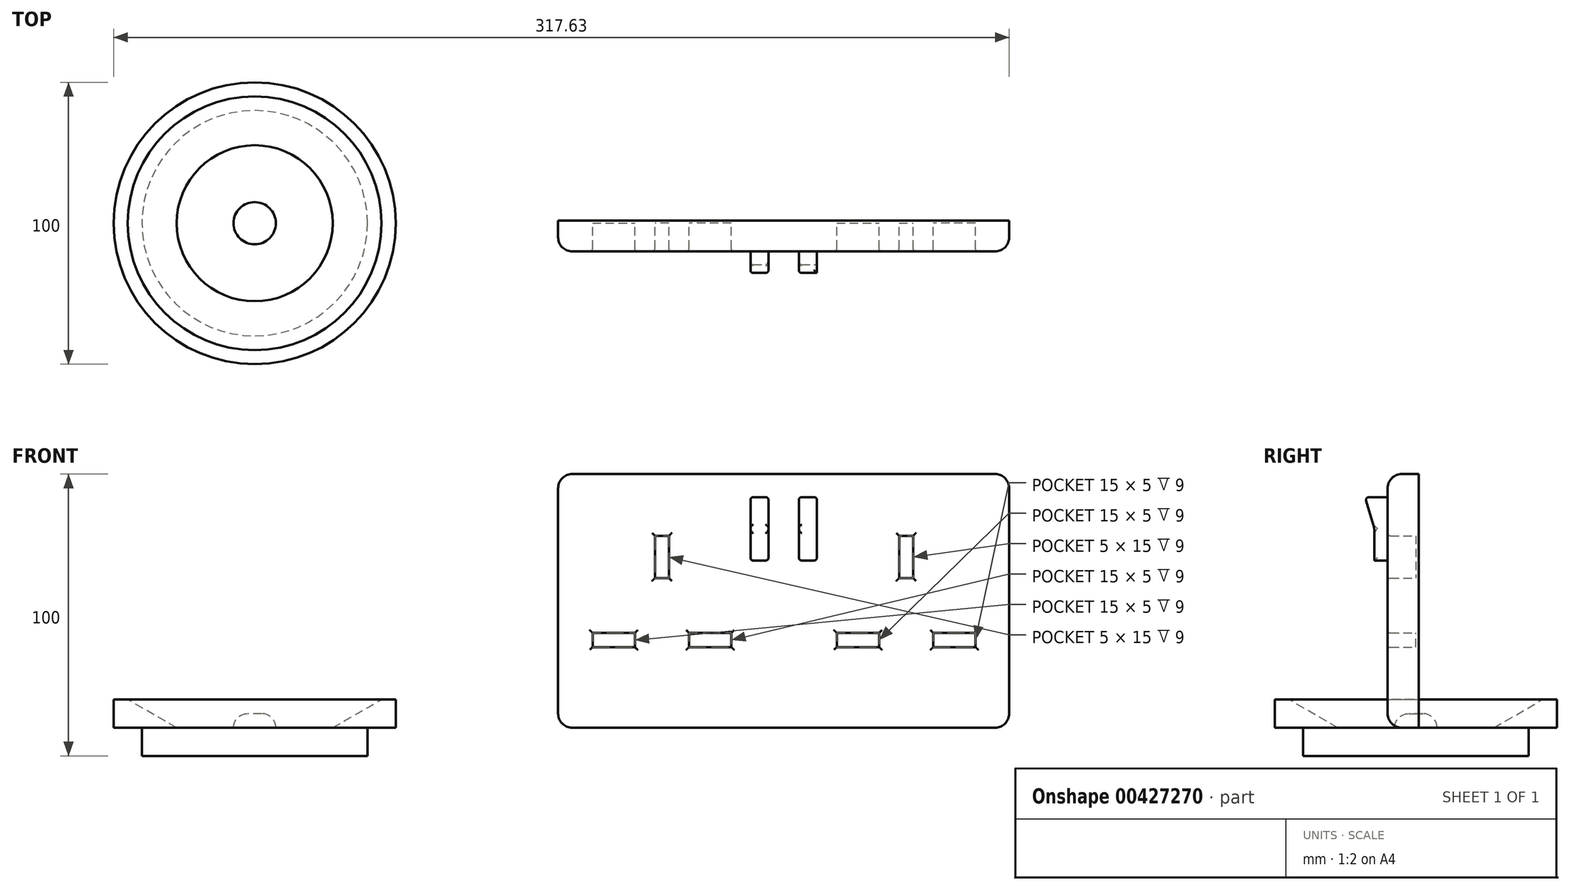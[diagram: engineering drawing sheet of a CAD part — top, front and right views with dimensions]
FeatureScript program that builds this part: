
annotation { "Feature Type Name" : "Feature", "Feature Type Description" : "" }
export const myFeature = defineFeature(function(context is Context, id is Id, definition is map)
    precondition{}
    {
        {
            var Q0;
            Q0=qCreatedBy(makeId("Top.planeOp"),FACE);
            var sketch = newSketch(context, id + "F0", { "sketchPlane" : qUnion([Q0])});
            skCircle(sketch, "E0", {"center": v(0, 0) * mm, "radius": 50 * mm});
            skSolve(sketch);
        }
        {
            var Q0;
            Q0 = qSketchRegion(id + "F0", true);
            extrude(context, id + "F1", {"entities" : qUnion([Q0]), "depth" : 10 * mm, "offsetDistance" : 25 * mm});
        }
        {
            var Q0;
            Q0=makeQuery(id+"F1.opExtrude","CAP_FACE",FACE,{"disambiguationData":[OSD([sQuery(id+"F0.wireOp",EDGE,"E0")])],"isStart":true});
            var sketch = newSketch(context, id + "F2", { "sketchPlane" : qUnion([Q0])});
            skCircle(sketch, "E1", {"center": v(0, 0) * mm, "radius": 40 * mm});
            skSolve(sketch);
        }
        {
            var Q0;
            Q0 = qSketchRegion(id + "F2", true);
            extrude(context, id + "F3", {"entities" : qUnion([Q0]), "operationType" : NewBodyOperationType.ADD, "depth" : 10 * mm, "offsetDistance" : 25 * mm});
        }
        {
            var Q0;
            Q0=makeQuery(id+"F1.opExtrude","CAP_FACE",FACE,{"disambiguationData":[OSD([sQuery(id+"F0.wireOp",EDGE,"E0")])],"isStart":false});
            var sketch = newSketch(context, id + "F4", { "sketchPlane" : qUnion([Q0])});
            skCircle(sketch, "E2", {"center": v(0, 0) * mm, "radius": 45 * mm});
            skSolve(sketch);
        }
        {
            var Q0;
            Q0 = qSketchRegion(id + "F4", true);
            extrude(context, id + "F5", {"entities" : qUnion([Q0]), "operationType" : NewBodyOperationType.REMOVE, "oppositeDirection" : true, "depth" : 10 * mm, "offsetDistance" : 25 * mm, "hasDraft" : true, "draftAngle" : 60 * degree, "draftPullDirection" : true});
        }
        {
            var Q0;
            Q0=makeQuery(id+"F5.boolean.opBoolean","COPY",FACE,{"derivedFrom":makeQuery(id+"F5.opExtrude","CAP_FACE",FACE,{"disambiguationData":[OSD([sQuery(id+"F4.wireOp",EDGE,"E2")])],"isStart":false})});
            var sketch = newSketch(context, id + "F6", { "sketchPlane" : qUnion([Q0])});
            skCircle(sketch, "E3", {"center": v(0, 0) * mm, "radius": 7.5 * mm});
            skSolve(sketch);
        }
        {
            var Q0;
            Q0 = qSketchRegion(id + "F6", true);
            extrude(context, id + "F7", {"entities" : qUnion([Q0]), "operationType" : NewBodyOperationType.ADD, "depth" : 5 * mm, "offsetDistance" : 25 * mm});
        }
        {
            var Q0;
            Q0=makeQuery(id+"F7.opExtrude","CAP_EDGE",EDGE,{"disambiguationData":[OSD([sQuery(id+"F6.wireOp",EDGE,"E3")])],"isStart":false});
            fillet(context, id + "F8", {"entities" : qUnion([Q0]), "radius" : 5 * mm, "tangentPropagation" : true, "allowEdgeOverflow" : false});
        }
        {
            var Q0;
            Q0=qCreatedBy(makeId("Front.planeOp"),FACE);
            var sketch = newSketch(context, id + "F9", { "sketchPlane" : qUnion([Q0])});
            skLineSegment(sketch, "E4.bottom", {"start": v(107.63, 0) * mm, "end": v(267.63, 0) * mm});
            skLineSegment(sketch, "E4.top", {"start": v(107.63, 90) * mm, "end": v(267.63, 90) * mm});
            skLineSegment(sketch, "E4.left", {"start": v(107.63, 0) * mm, "end": v(107.63, 90) * mm});
            skLineSegment(sketch, "E4.right", {"start": v(267.63, 0) * mm, "end": v(267.63, 90) * mm});
            skSolve(sketch);
        }
        {
            var Q0;
            Q0 = qSketchRegion(id + "F9", true);
            extrude(context, id + "F10", {"entities" : qUnion([Q0]), "depth" : 10 * mm, "offsetDistance" : 25 * mm});
        }
        {
            var Q0;
            Q0=qCreatedBy(makeId("Front.planeOp"),FACE);
            var sketch = newSketch(context, id + "F11", { "sketchPlane" : qUnion([Q0])});
            skLineSegment(sketch, "E5.bottom", {"start": v(146.96, 68.1) * mm, "end": v(141.96, 68.1) * mm});
            skLineSegment(sketch, "E5.top", {"start": v(146.96, 53.1) * mm, "end": v(141.96, 53.1) * mm});
            skLineSegment(sketch, "E5.left", {"start": v(146.96, 68.1) * mm, "end": v(146.96, 53.1) * mm});
            skLineSegment(sketch, "E5.right", {"start": v(141.96, 68.1) * mm, "end": v(141.96, 53.1) * mm});
            skPoint(sketch, "E5.middle", {"position": v(144.46, 60.6) * mm});
            skLineSegment(sketch, "E6.bottom", {"start": v(119.85, 28.62) * mm, "end": v(134.85, 28.62) * mm});
            skLineSegment(sketch, "E6.top", {"start": v(119.85, 33.62) * mm, "end": v(134.85, 33.62) * mm});
            skLineSegment(sketch, "E6.left", {"start": v(119.85, 28.62) * mm, "end": v(119.85, 33.62) * mm});
            skLineSegment(sketch, "E6.right", {"start": v(134.85, 28.62) * mm, "end": v(134.85, 33.62) * mm});
            skPoint(sketch, "E6.middle", {"position": v(127.35, 31.12) * mm});
            skLineSegment(sketch, "E7.bottom", {"start": v(169.06, 28.62) * mm, "end": v(154.06, 28.62) * mm});
            skLineSegment(sketch, "E7.top", {"start": v(169.06, 33.62) * mm, "end": v(154.06, 33.62) * mm});
            skLineSegment(sketch, "E7.left", {"start": v(169.06, 28.62) * mm, "end": v(169.06, 33.62) * mm});
            skLineSegment(sketch, "E7.right", {"start": v(154.06, 28.62) * mm, "end": v(154.06, 33.62) * mm});
            skPoint(sketch, "E7.middle", {"position": v(161.56, 31.12) * mm});
            skPoint(sketch, "E8", {"position": v(134.85, 31.12) * mm});
            skLineSegment(sketch, "E9.MirrorCS", {"start": v(228.58, 68.1) * mm, "end": v(228.58, 53.1) * mm});
            skLineSegment(sketch, "E10.MirrorCS", {"start": v(228.58, 68.1) * mm, "end": v(233.58, 68.1) * mm});
            skLineSegment(sketch, "E11.MirrorCS", {"start": v(233.58, 68.1) * mm, "end": v(233.58, 53.1) * mm});
            skLineSegment(sketch, "E12.MirrorCS", {"start": v(228.58, 53.1) * mm, "end": v(233.58, 53.1) * mm});
            skLineSegment(sketch, "E13.MirrorCS", {"start": v(206.47, 28.62) * mm, "end": v(221.47, 28.62) * mm});
            skLineSegment(sketch, "E14.MirrorCS", {"start": v(206.47, 33.62) * mm, "end": v(221.47, 33.62) * mm});
            skLineSegment(sketch, "E15.MirrorCS", {"start": v(221.47, 28.62) * mm, "end": v(221.47, 33.62) * mm});
            skLineSegment(sketch, "E16.MirrorCS", {"start": v(206.47, 28.62) * mm, "end": v(206.47, 33.62) * mm});
            skPoint(sketch, "E17.MirrorP", {"position": v(213.97, 31.12) * mm});
            skLineSegment(sketch, "E18.MirrorCS", {"start": v(240.68, 28.62) * mm, "end": v(240.68, 33.62) * mm});
            skLineSegment(sketch, "E19.MirrorCS", {"start": v(255.68, 28.62) * mm, "end": v(255.68, 33.62) * mm});
            skLineSegment(sketch, "E20.MirrorCS", {"start": v(255.68, 28.62) * mm, "end": v(240.68, 28.62) * mm});
            skLineSegment(sketch, "E21.MirrorCS", {"start": v(255.68, 33.62) * mm, "end": v(240.68, 33.62) * mm});
            skPoint(sketch, "E22.MirrorP", {"position": v(248.18, 31.12) * mm});
            skPoint(sketch, "E23.MirrorP", {"position": v(240.68, 31.12) * mm});
            skSolve(sketch);
        }
        {
            var Q0;
            Q0 = qSketchRegion(id + "F11", true);
            extrude(context, id + "F12", {"entities" : qUnion([Q0]), "operationType" : NewBodyOperationType.REMOVE, "depth" : 15 * mm, "offsetDistance" : 25 * mm});
        }
        {
            var Q0;
            Q0=makeQuery(id+"F10.opExtrude","CAP_FACE",FACE,{"disambiguationData":[OSD([sQuery(id+"F9.wireOp",EDGE,"E4.bottom"),sQuery(id+"F9.wireOp",EDGE,"E4.top"),sQuery(id+"F9.wireOp",EDGE,"E4.left"),sQuery(id+"F9.wireOp",EDGE,"E4.right")])],"isStart":false});
            var sketch = newSketch(context, id + "F13", { "sketchPlane" : qUnion([Q0])});
            skLineSegment(sketch, "E24.bottom", {"start": v(193.04, 81.81) * mm, "end": v(199.4, 81.81) * mm});
            skLineSegment(sketch, "E24.top", {"start": v(193.04, 59.31) * mm, "end": v(199.4, 59.31) * mm});
            skLineSegment(sketch, "E24.left", {"start": v(193.04, 81.81) * mm, "end": v(193.04, 59.31) * mm});
            skLineSegment(sketch, "E24.right", {"start": v(199.4, 81.81) * mm, "end": v(199.4, 59.31) * mm});
            skLineSegment(sketch, "E25.MirrorCS", {"start": v(182.22, 81.81) * mm, "end": v(175.86, 81.81) * mm});
            skLineSegment(sketch, "E26.MirrorCS", {"start": v(182.22, 81.81) * mm, "end": v(182.22, 59.31) * mm});
            skLineSegment(sketch, "E27.MirrorCS", {"start": v(175.86, 81.81) * mm, "end": v(175.86, 59.31) * mm});
            skLineSegment(sketch, "E28.MirrorCS", {"start": v(182.22, 59.31) * mm, "end": v(175.86, 59.31) * mm});
            skSolve(sketch);
        }
        {
            var Q0;
            Q0 = qSketchRegion(id + "F13", true);
            extrude(context, id + "F14", {"entities" : qUnion([Q0]), "operationType" : NewBodyOperationType.ADD, "depth" : 8 * mm, "offsetDistance" : 25 * mm});
        }
        {
            var Q0;
            Q0=makeQuery(id+"F14.opExtrude","SWEPT_FACE",FACE,{"disambiguationData":[OSD([sQuery(id+"F13.wireOp",EDGE,"E24.right")])]});
            var sketch = newSketch(context, id + "F15", { "sketchPlane" : qUnion([Q0])});
            skLineSegment(sketch, "E29", {"start": v(-14.66, 70.56) * mm, "end": v(-18, 81.81) * mm});
            skLineSegment(sketch, "E30", {"start": v(-14.66, 70.56) * mm, "end": v(-14.66, 59.31) * mm});
            skPoint(sketch, "E30.endSnap0", {"position": v(-14, 59.31) * mm});
            skLineSegment(sketch, "E31", {"start": v(-14.66, 59.31) * mm, "end": v(-18, 59.31) * mm});
            skLineSegment(sketch, "E32", {"start": v(-18, 59.31) * mm, "end": v(-18, 81.81) * mm});
            skSolve(sketch);
        }
        {
            var Q0;
            Q0 = qSketchRegion(id + "F15", true);
            extrude(context, id + "F16", {"entities" : qUnion([Q0]), "operationType" : NewBodyOperationType.REMOVE, "oppositeDirection" : true, "depth" : 25 * mm, "offsetDistance" : 25 * mm});
        }
        {
            var Q0;
            Q0=makeQuery(id+"F16.boolean.opBoolean","COPY",EDGE,{"derivedFrom":makeQuery(id+"F16.opExtrude","CAP_EDGE",EDGE,{"disambiguationData":[OSD([sQuery(id+"F15.wireOp",EDGE,"E30")])],"isStart":true})});
            var Q1;
            Q1=makeQuery(id+"F16.boolean.opBoolean","COPY",EDGE,{"derivedFrom":makeQuery(id+"F16.opExtrude","CAP_EDGE",EDGE,{"disambiguationData":[OSD([sQuery(id+"F15.wireOp",EDGE,"E29")])],"isStart":true})});
            var Q2;
            {var subQ0=sQuery(id+"F13.wireOp",EDGE,"E24.bottom");Q2=makeQuery(id+"F16.boolean.opBoolean","MERGE",EDGE,{"derivedFrom":[makeQuery(id+"F14.opExtrude","CAP_EDGE",EDGE,{"disambiguationData":[OSD([subQ0])],"isStart":false}),makeQuery(id+"F16.opExtrude","SWEPT_EDGE",EDGE,{"disambiguationData":[OSD([subQ0,sQuery(id+"F13.wireOp",EDGE,"E24.right"),sQuery(id+"F15.wireOp",EDGE,"E29"),sQuery(id+"F15.wireOp",EDGE,"E32")])]})]});}
            var Q3;
            Q3=makeQuery(id+"F16.boolean.opBoolean","INTERSECT",EDGE,{"derivedFrom":[makeQuery(id+"F14.opExtrude","SWEPT_FACE",FACE,{"disambiguationData":[OSD([sQuery(id+"F13.wireOp",EDGE,"E24.left")])]}),makeQuery(id+"F16.opExtrude","SWEPT_FACE",FACE,{"disambiguationData":[OSD([sQuery(id+"F15.wireOp",EDGE,"E29")])]})]});
            var Q4;
            Q4=makeQuery(id+"F16.boolean.opBoolean","INTERSECT",EDGE,{"derivedFrom":[makeQuery(id+"F14.opExtrude","SWEPT_FACE",FACE,{"disambiguationData":[OSD([sQuery(id+"F13.wireOp",EDGE,"E24.left")])]}),makeQuery(id+"F16.opExtrude","SWEPT_FACE",FACE,{"disambiguationData":[OSD([sQuery(id+"F15.wireOp",EDGE,"E30")])]})]});
            var Q5;
            {var subQ0=sQuery(id+"F13.wireOp",EDGE,"E24.top");var subQ1=sQuery(id+"F15.wireOp",EDGE,"E30");Q5=makeQuery(id+"F16.boolean.opBoolean","COPY",EDGE,{"disambiguationData":[topologyDisambiguationEdgeConnected([makeQuery(id+"F14.opExtrude","SWEPT_FACE",FACE,{"disambiguationData":[OSD([subQ0])]})])],"derivedFrom":makeQuery(id+"F16.opExtrude","SWEPT_EDGE",EDGE,{"disambiguationData":[OSD([subQ0,sQuery(id+"F13.wireOp",EDGE,"E24.right"),subQ1,sQuery(id+"F15.wireOp",EDGE,"E31")])]})});}
            var Q6;
            Q6=makeQuery(id+"F14.opExtrude","SWEPT_EDGE",EDGE,{"disambiguationData":[OSD([sQuery(id+"F13.wireOp",EDGE,"E24.bottom"),sQuery(id+"F13.wireOp",EDGE,"E24.right")])]});
            var Q7;
            Q7=makeQuery(id+"F14.opExtrude","SWEPT_EDGE",EDGE,{"disambiguationData":[OSD([sQuery(id+"F13.wireOp",EDGE,"E24.top"),sQuery(id+"F13.wireOp",EDGE,"E24.right")])]});
            var Q8;
            Q8=makeQuery(id+"F14.opExtrude","SWEPT_EDGE",EDGE,{"disambiguationData":[OSD([sQuery(id+"F13.wireOp",EDGE,"E24.top"),sQuery(id+"F13.wireOp",EDGE,"E24.left")])]});
            var Q9;
            Q9=makeQuery(id+"F14.opExtrude","SWEPT_EDGE",EDGE,{"disambiguationData":[OSD([sQuery(id+"F13.wireOp",EDGE,"E24.bottom"),sQuery(id+"F13.wireOp",EDGE,"E24.left")])]});
            var Q10;
            Q10=makeQuery(id+"F16.boolean.opBoolean","INTERSECT",EDGE,{"derivedFrom":[makeQuery(id+"F14.opExtrude","SWEPT_FACE",FACE,{"disambiguationData":[OSD([sQuery(id+"F13.wireOp",EDGE,"E26.MirrorCS")])]}),makeQuery(id+"F16.opExtrude","SWEPT_FACE",FACE,{"disambiguationData":[OSD([sQuery(id+"F15.wireOp",EDGE,"E30")])]})]});
            var Q11;
            Q11=makeQuery(id+"F16.boolean.opBoolean","INTERSECT",EDGE,{"derivedFrom":[makeQuery(id+"F14.opExtrude","SWEPT_FACE",FACE,{"disambiguationData":[OSD([sQuery(id+"F13.wireOp",EDGE,"E26.MirrorCS")])]}),makeQuery(id+"F16.opExtrude","SWEPT_FACE",FACE,{"disambiguationData":[OSD([sQuery(id+"F15.wireOp",EDGE,"E29")])]})]});
            var Q12;
            Q12=makeQuery(id+"F16.boolean.opBoolean","MERGE",EDGE,{"derivedFrom":[makeQuery(id+"F14.opExtrude","CAP_EDGE",EDGE,{"disambiguationData":[OSD([sQuery(id+"F13.wireOp",EDGE,"E25.MirrorCS")])],"isStart":false}),makeQuery(id+"F16.opExtrude","SWEPT_EDGE",EDGE,{"disambiguationData":[OSD([sQuery(id+"F13.wireOp",EDGE,"E24.bottom"),sQuery(id+"F13.wireOp",EDGE,"E24.right"),sQuery(id+"F15.wireOp",EDGE,"E29"),sQuery(id+"F15.wireOp",EDGE,"E32")])]})]});
            var Q13;
            Q13=makeQuery(id+"F16.boolean.opBoolean","INTERSECT",EDGE,{"derivedFrom":[makeQuery(id+"F14.opExtrude","SWEPT_FACE",FACE,{"disambiguationData":[OSD([sQuery(id+"F13.wireOp",EDGE,"E27.MirrorCS")])]}),makeQuery(id+"F16.opExtrude","SWEPT_FACE",FACE,{"disambiguationData":[OSD([sQuery(id+"F15.wireOp",EDGE,"E29")])]})]});
            var Q14;
            Q14=makeQuery(id+"F16.boolean.opBoolean","INTERSECT",EDGE,{"derivedFrom":[makeQuery(id+"F14.opExtrude","SWEPT_FACE",FACE,{"disambiguationData":[OSD([sQuery(id+"F13.wireOp",EDGE,"E27.MirrorCS")])]}),makeQuery(id+"F16.opExtrude","SWEPT_FACE",FACE,{"disambiguationData":[OSD([sQuery(id+"F15.wireOp",EDGE,"E30")])]})]});
            var Q15;
            {var subQ0=sQuery(id+"F15.wireOp",EDGE,"E30");Q15=makeQuery(id+"F16.boolean.opBoolean","COPY",EDGE,{"disambiguationData":[topologyDisambiguationEdgeConnected([makeQuery(id+"F14.opExtrude","SWEPT_FACE",FACE,{"disambiguationData":[OSD([sQuery(id+"F13.wireOp",EDGE,"E28.MirrorCS")])]})])],"derivedFrom":makeQuery(id+"F16.opExtrude","SWEPT_EDGE",EDGE,{"disambiguationData":[OSD([sQuery(id+"F13.wireOp",EDGE,"E24.top"),sQuery(id+"F13.wireOp",EDGE,"E24.right"),subQ0,sQuery(id+"F15.wireOp",EDGE,"E31")])]})});}
            var Q16;
            Q16=makeQuery(id+"F14.opExtrude","SWEPT_EDGE",EDGE,{"disambiguationData":[OSD([sQuery(id+"F13.wireOp",EDGE,"E27.MirrorCS"),sQuery(id+"F13.wireOp",EDGE,"E28.MirrorCS")])]});
            var Q17;
            Q17=makeQuery(id+"F14.opExtrude","SWEPT_EDGE",EDGE,{"disambiguationData":[OSD([sQuery(id+"F13.wireOp",EDGE,"E26.MirrorCS"),sQuery(id+"F13.wireOp",EDGE,"E28.MirrorCS")])]});
            var Q18;
            Q18=makeQuery(id+"F14.opExtrude","SWEPT_EDGE",EDGE,{"disambiguationData":[OSD([sQuery(id+"F13.wireOp",EDGE,"E25.MirrorCS"),sQuery(id+"F13.wireOp",EDGE,"E26.MirrorCS")])]});
            var Q19;
            Q19=makeQuery(id+"F14.opExtrude","SWEPT_EDGE",EDGE,{"disambiguationData":[OSD([sQuery(id+"F13.wireOp",EDGE,"E25.MirrorCS"),sQuery(id+"F13.wireOp",EDGE,"E27.MirrorCS")])]});
            fillet(context, id + "F17", {"entities" : qUnion([Q0, Q1, Q2, Q3, Q4, Q5, Q6, Q7, Q8, Q9, Q10, Q11, Q12, Q13, Q14, Q15, Q16, Q17, Q18, Q19]), "radius" : 1 * mm, "tangentPropagation" : true, "allowEdgeOverflow" : false});
        }
        {
            var Q0;
            {var subQ0=sQuery(id+"F15.wireOp",EDGE,"E29");var subQ1=sQuery(id+"F15.wireOp",EDGE,"E30");Q0=makeQuery(id+"F16.boolean.opBoolean","COPY",EDGE,{"disambiguationData":[TD([makeQuery(id+"F14.opExtrude","SWEPT_FACE",FACE,{"disambiguationData":[OSD([sQuery(id+"F13.wireOp",EDGE,"E26.MirrorCS")])]})])],"derivedFrom":makeQuery(id+"F16.opExtrude","SWEPT_EDGE",EDGE,{"disambiguationData":[OSD([subQ0,subQ1])]})});}
            var Q1;
            {var subQ0=sQuery(id+"F15.wireOp",EDGE,"E29");var subQ1=sQuery(id+"F15.wireOp",EDGE,"E30");Q1=makeQuery(id+"F16.boolean.opBoolean","COPY",EDGE,{"disambiguationData":[TD([makeQuery(id+"F14.opExtrude","SWEPT_FACE",FACE,{"disambiguationData":[OSD([sQuery(id+"F13.wireOp",EDGE,"E24.left")])]})])],"derivedFrom":makeQuery(id+"F16.opExtrude","SWEPT_EDGE",EDGE,{"disambiguationData":[OSD([subQ0,subQ1])]})});}
            fillet(context, id + "F18", {"entities" : qUnion([Q0, Q1]), "radius" : 10 * mm, "tangentPropagation" : true, "allowEdgeOverflow" : false});
        }
        {
            var Q0;
            Q0=makeQuery(id+"F12.boolean.opBoolean","INTERSECT",EDGE,{"derivedFrom":[makeQuery(id+"F10.opExtrude","CAP_FACE",FACE,{"disambiguationData":[OSD([sQuery(id+"F9.wireOp",EDGE,"E4.bottom"),sQuery(id+"F9.wireOp",EDGE,"E4.top"),sQuery(id+"F9.wireOp",EDGE,"E4.left"),sQuery(id+"F9.wireOp",EDGE,"E4.right")])],"isStart":false}),makeQuery(id+"F12.opExtrude","SWEPT_FACE",FACE,{"disambiguationData":[OSD([sQuery(id+"F11.wireOp",EDGE,"E5.right")])]})]});
            var Q1;
            Q1=makeQuery(id+"F12.boolean.opBoolean","INTERSECT",EDGE,{"derivedFrom":[makeQuery(id+"F10.opExtrude","CAP_FACE",FACE,{"disambiguationData":[OSD([sQuery(id+"F9.wireOp",EDGE,"E4.bottom"),sQuery(id+"F9.wireOp",EDGE,"E4.top"),sQuery(id+"F9.wireOp",EDGE,"E4.left"),sQuery(id+"F9.wireOp",EDGE,"E4.right")])],"isStart":false}),makeQuery(id+"F12.opExtrude","SWEPT_FACE",FACE,{"disambiguationData":[OSD([sQuery(id+"F11.wireOp",EDGE,"E5.top")])]})]});
            var Q2;
            Q2=makeQuery(id+"F12.boolean.opBoolean","INTERSECT",EDGE,{"derivedFrom":[makeQuery(id+"F10.opExtrude","CAP_FACE",FACE,{"disambiguationData":[OSD([sQuery(id+"F9.wireOp",EDGE,"E4.bottom"),sQuery(id+"F9.wireOp",EDGE,"E4.top"),sQuery(id+"F9.wireOp",EDGE,"E4.left"),sQuery(id+"F9.wireOp",EDGE,"E4.right")])],"isStart":false}),makeQuery(id+"F12.opExtrude","SWEPT_FACE",FACE,{"disambiguationData":[OSD([sQuery(id+"F11.wireOp",EDGE,"E5.left")])]})]});
            var Q3;
            Q3=makeQuery(id+"F12.boolean.opBoolean","INTERSECT",EDGE,{"derivedFrom":[makeQuery(id+"F10.opExtrude","CAP_FACE",FACE,{"disambiguationData":[OSD([sQuery(id+"F9.wireOp",EDGE,"E4.bottom"),sQuery(id+"F9.wireOp",EDGE,"E4.top"),sQuery(id+"F9.wireOp",EDGE,"E4.left"),sQuery(id+"F9.wireOp",EDGE,"E4.right")])],"isStart":false}),makeQuery(id+"F12.opExtrude","SWEPT_FACE",FACE,{"disambiguationData":[OSD([sQuery(id+"F11.wireOp",EDGE,"E5.bottom")])]})]});
            var Q4;
            Q4=makeQuery(id+"F12.boolean.opBoolean","INTERSECT",EDGE,{"derivedFrom":[makeQuery(id+"F10.opExtrude","CAP_FACE",FACE,{"disambiguationData":[OSD([sQuery(id+"F9.wireOp",EDGE,"E4.bottom"),sQuery(id+"F9.wireOp",EDGE,"E4.top"),sQuery(id+"F9.wireOp",EDGE,"E4.left"),sQuery(id+"F9.wireOp",EDGE,"E4.right")])],"isStart":false}),makeQuery(id+"F12.opExtrude","SWEPT_FACE",FACE,{"disambiguationData":[OSD([sQuery(id+"F11.wireOp",EDGE,"E6.top")])]})]});
            var Q5;
            Q5=makeQuery(id+"F12.boolean.opBoolean","INTERSECT",EDGE,{"derivedFrom":[makeQuery(id+"F10.opExtrude","CAP_FACE",FACE,{"disambiguationData":[OSD([sQuery(id+"F9.wireOp",EDGE,"E4.bottom"),sQuery(id+"F9.wireOp",EDGE,"E4.top"),sQuery(id+"F9.wireOp",EDGE,"E4.left"),sQuery(id+"F9.wireOp",EDGE,"E4.right")])],"isStart":false}),makeQuery(id+"F12.opExtrude","SWEPT_FACE",FACE,{"disambiguationData":[OSD([sQuery(id+"F11.wireOp",EDGE,"E6.left")])]})]});
            var Q6;
            Q6=makeQuery(id+"F12.boolean.opBoolean","INTERSECT",EDGE,{"derivedFrom":[makeQuery(id+"F10.opExtrude","CAP_FACE",FACE,{"disambiguationData":[OSD([sQuery(id+"F9.wireOp",EDGE,"E4.bottom"),sQuery(id+"F9.wireOp",EDGE,"E4.top"),sQuery(id+"F9.wireOp",EDGE,"E4.left"),sQuery(id+"F9.wireOp",EDGE,"E4.right")])],"isStart":false}),makeQuery(id+"F12.opExtrude","SWEPT_FACE",FACE,{"disambiguationData":[OSD([sQuery(id+"F11.wireOp",EDGE,"E6.bottom")])]})]});
            var Q7;
            Q7=makeQuery(id+"F12.boolean.opBoolean","INTERSECT",EDGE,{"derivedFrom":[makeQuery(id+"F10.opExtrude","CAP_FACE",FACE,{"disambiguationData":[OSD([sQuery(id+"F9.wireOp",EDGE,"E4.bottom"),sQuery(id+"F9.wireOp",EDGE,"E4.top"),sQuery(id+"F9.wireOp",EDGE,"E4.left"),sQuery(id+"F9.wireOp",EDGE,"E4.right")])],"isStart":false}),makeQuery(id+"F12.opExtrude","SWEPT_FACE",FACE,{"disambiguationData":[OSD([sQuery(id+"F11.wireOp",EDGE,"E6.right")])]})]});
            var Q8;
            Q8=makeQuery(id+"F12.boolean.opBoolean","INTERSECT",EDGE,{"derivedFrom":[makeQuery(id+"F10.opExtrude","CAP_FACE",FACE,{"disambiguationData":[OSD([sQuery(id+"F9.wireOp",EDGE,"E4.bottom"),sQuery(id+"F9.wireOp",EDGE,"E4.top"),sQuery(id+"F9.wireOp",EDGE,"E4.left"),sQuery(id+"F9.wireOp",EDGE,"E4.right")])],"isStart":false}),makeQuery(id+"F12.opExtrude","SWEPT_FACE",FACE,{"disambiguationData":[OSD([sQuery(id+"F11.wireOp",EDGE,"E7.right")])]})]});
            var Q9;
            Q9=makeQuery(id+"F12.boolean.opBoolean","INTERSECT",EDGE,{"derivedFrom":[makeQuery(id+"F10.opExtrude","CAP_FACE",FACE,{"disambiguationData":[OSD([sQuery(id+"F9.wireOp",EDGE,"E4.bottom"),sQuery(id+"F9.wireOp",EDGE,"E4.top"),sQuery(id+"F9.wireOp",EDGE,"E4.left"),sQuery(id+"F9.wireOp",EDGE,"E4.right")])],"isStart":false}),makeQuery(id+"F12.opExtrude","SWEPT_FACE",FACE,{"disambiguationData":[OSD([sQuery(id+"F11.wireOp",EDGE,"E7.top")])]})]});
            var Q10;
            Q10=makeQuery(id+"F12.boolean.opBoolean","INTERSECT",EDGE,{"derivedFrom":[makeQuery(id+"F10.opExtrude","CAP_FACE",FACE,{"disambiguationData":[OSD([sQuery(id+"F9.wireOp",EDGE,"E4.bottom"),sQuery(id+"F9.wireOp",EDGE,"E4.top"),sQuery(id+"F9.wireOp",EDGE,"E4.left"),sQuery(id+"F9.wireOp",EDGE,"E4.right")])],"isStart":false}),makeQuery(id+"F12.opExtrude","SWEPT_FACE",FACE,{"disambiguationData":[OSD([sQuery(id+"F11.wireOp",EDGE,"E7.left")])]})]});
            var Q11;
            Q11=makeQuery(id+"F12.boolean.opBoolean","INTERSECT",EDGE,{"derivedFrom":[makeQuery(id+"F10.opExtrude","CAP_FACE",FACE,{"disambiguationData":[OSD([sQuery(id+"F9.wireOp",EDGE,"E4.bottom"),sQuery(id+"F9.wireOp",EDGE,"E4.top"),sQuery(id+"F9.wireOp",EDGE,"E4.left"),sQuery(id+"F9.wireOp",EDGE,"E4.right")])],"isStart":false}),makeQuery(id+"F12.opExtrude","SWEPT_FACE",FACE,{"disambiguationData":[OSD([sQuery(id+"F11.wireOp",EDGE,"E7.bottom")])]})]});
            var Q12;
            Q12=makeQuery(id+"F12.boolean.opBoolean","INTERSECT",EDGE,{"derivedFrom":[makeQuery(id+"F10.opExtrude","CAP_FACE",FACE,{"disambiguationData":[OSD([sQuery(id+"F9.wireOp",EDGE,"E4.bottom"),sQuery(id+"F9.wireOp",EDGE,"E4.top"),sQuery(id+"F9.wireOp",EDGE,"E4.left"),sQuery(id+"F9.wireOp",EDGE,"E4.right")])],"isStart":false}),makeQuery(id+"F12.opExtrude","SWEPT_FACE",FACE,{"disambiguationData":[OSD([sQuery(id+"F11.wireOp",EDGE,"E13.MirrorCS")])]})]});
            var Q13;
            Q13=makeQuery(id+"F12.boolean.opBoolean","INTERSECT",EDGE,{"derivedFrom":[makeQuery(id+"F10.opExtrude","CAP_FACE",FACE,{"disambiguationData":[OSD([sQuery(id+"F9.wireOp",EDGE,"E4.bottom"),sQuery(id+"F9.wireOp",EDGE,"E4.top"),sQuery(id+"F9.wireOp",EDGE,"E4.left"),sQuery(id+"F9.wireOp",EDGE,"E4.right")])],"isStart":false}),makeQuery(id+"F12.opExtrude","SWEPT_FACE",FACE,{"disambiguationData":[OSD([sQuery(id+"F11.wireOp",EDGE,"E14.MirrorCS")])]})]});
            var Q14;
            Q14=makeQuery(id+"F12.boolean.opBoolean","INTERSECT",EDGE,{"derivedFrom":[makeQuery(id+"F10.opExtrude","CAP_FACE",FACE,{"disambiguationData":[OSD([sQuery(id+"F9.wireOp",EDGE,"E4.bottom"),sQuery(id+"F9.wireOp",EDGE,"E4.top"),sQuery(id+"F9.wireOp",EDGE,"E4.left"),sQuery(id+"F9.wireOp",EDGE,"E4.right")])],"isStart":false}),makeQuery(id+"F12.opExtrude","SWEPT_FACE",FACE,{"disambiguationData":[OSD([sQuery(id+"F11.wireOp",EDGE,"E16.MirrorCS")])]})]});
            var Q15;
            Q15=makeQuery(id+"F12.boolean.opBoolean","INTERSECT",EDGE,{"derivedFrom":[makeQuery(id+"F10.opExtrude","CAP_FACE",FACE,{"disambiguationData":[OSD([sQuery(id+"F9.wireOp",EDGE,"E4.bottom"),sQuery(id+"F9.wireOp",EDGE,"E4.top"),sQuery(id+"F9.wireOp",EDGE,"E4.left"),sQuery(id+"F9.wireOp",EDGE,"E4.right")])],"isStart":false}),makeQuery(id+"F12.opExtrude","SWEPT_FACE",FACE,{"disambiguationData":[OSD([sQuery(id+"F11.wireOp",EDGE,"E15.MirrorCS")])]})]});
            var Q16;
            Q16=makeQuery(id+"F12.boolean.opBoolean","INTERSECT",EDGE,{"derivedFrom":[makeQuery(id+"F10.opExtrude","CAP_FACE",FACE,{"disambiguationData":[OSD([sQuery(id+"F9.wireOp",EDGE,"E4.bottom"),sQuery(id+"F9.wireOp",EDGE,"E4.top"),sQuery(id+"F9.wireOp",EDGE,"E4.left"),sQuery(id+"F9.wireOp",EDGE,"E4.right")])],"isStart":false}),makeQuery(id+"F12.opExtrude","SWEPT_FACE",FACE,{"disambiguationData":[OSD([sQuery(id+"F11.wireOp",EDGE,"E21.MirrorCS")])]})]});
            var Q17;
            Q17=makeQuery(id+"F12.boolean.opBoolean","INTERSECT",EDGE,{"derivedFrom":[makeQuery(id+"F10.opExtrude","CAP_FACE",FACE,{"disambiguationData":[OSD([sQuery(id+"F9.wireOp",EDGE,"E4.bottom"),sQuery(id+"F9.wireOp",EDGE,"E4.top"),sQuery(id+"F9.wireOp",EDGE,"E4.left"),sQuery(id+"F9.wireOp",EDGE,"E4.right")])],"isStart":false}),makeQuery(id+"F12.opExtrude","SWEPT_FACE",FACE,{"disambiguationData":[OSD([sQuery(id+"F11.wireOp",EDGE,"E18.MirrorCS")])]})]});
            var Q18;
            Q18=makeQuery(id+"F12.boolean.opBoolean","INTERSECT",EDGE,{"derivedFrom":[makeQuery(id+"F10.opExtrude","CAP_FACE",FACE,{"disambiguationData":[OSD([sQuery(id+"F9.wireOp",EDGE,"E4.bottom"),sQuery(id+"F9.wireOp",EDGE,"E4.top"),sQuery(id+"F9.wireOp",EDGE,"E4.left"),sQuery(id+"F9.wireOp",EDGE,"E4.right")])],"isStart":false}),makeQuery(id+"F12.opExtrude","SWEPT_FACE",FACE,{"disambiguationData":[OSD([sQuery(id+"F11.wireOp",EDGE,"E20.MirrorCS")])]})]});
            var Q19;
            Q19=makeQuery(id+"F12.boolean.opBoolean","INTERSECT",EDGE,{"derivedFrom":[makeQuery(id+"F10.opExtrude","CAP_FACE",FACE,{"disambiguationData":[OSD([sQuery(id+"F9.wireOp",EDGE,"E4.bottom"),sQuery(id+"F9.wireOp",EDGE,"E4.top"),sQuery(id+"F9.wireOp",EDGE,"E4.left"),sQuery(id+"F9.wireOp",EDGE,"E4.right")])],"isStart":false}),makeQuery(id+"F12.opExtrude","SWEPT_FACE",FACE,{"disambiguationData":[OSD([sQuery(id+"F11.wireOp",EDGE,"E19.MirrorCS")])]})]});
            var Q20;
            Q20=makeQuery(id+"F12.boolean.opBoolean","INTERSECT",EDGE,{"derivedFrom":[makeQuery(id+"F10.opExtrude","CAP_FACE",FACE,{"disambiguationData":[OSD([sQuery(id+"F9.wireOp",EDGE,"E4.bottom"),sQuery(id+"F9.wireOp",EDGE,"E4.top"),sQuery(id+"F9.wireOp",EDGE,"E4.left"),sQuery(id+"F9.wireOp",EDGE,"E4.right")])],"isStart":false}),makeQuery(id+"F12.opExtrude","SWEPT_FACE",FACE,{"disambiguationData":[OSD([sQuery(id+"F11.wireOp",EDGE,"E10.MirrorCS")])]})]});
            var Q21;
            Q21=makeQuery(id+"F12.boolean.opBoolean","INTERSECT",EDGE,{"derivedFrom":[makeQuery(id+"F10.opExtrude","CAP_FACE",FACE,{"disambiguationData":[OSD([sQuery(id+"F9.wireOp",EDGE,"E4.bottom"),sQuery(id+"F9.wireOp",EDGE,"E4.top"),sQuery(id+"F9.wireOp",EDGE,"E4.left"),sQuery(id+"F9.wireOp",EDGE,"E4.right")])],"isStart":false}),makeQuery(id+"F12.opExtrude","SWEPT_FACE",FACE,{"disambiguationData":[OSD([sQuery(id+"F11.wireOp",EDGE,"E9.MirrorCS")])]})]});
            var Q22;
            Q22=makeQuery(id+"F12.boolean.opBoolean","INTERSECT",EDGE,{"derivedFrom":[makeQuery(id+"F10.opExtrude","CAP_FACE",FACE,{"disambiguationData":[OSD([sQuery(id+"F9.wireOp",EDGE,"E4.bottom"),sQuery(id+"F9.wireOp",EDGE,"E4.top"),sQuery(id+"F9.wireOp",EDGE,"E4.left"),sQuery(id+"F9.wireOp",EDGE,"E4.right")])],"isStart":false}),makeQuery(id+"F12.opExtrude","SWEPT_FACE",FACE,{"disambiguationData":[OSD([sQuery(id+"F11.wireOp",EDGE,"E12.MirrorCS")])]})]});
            var Q23;
            Q23=makeQuery(id+"F12.boolean.opBoolean","INTERSECT",EDGE,{"derivedFrom":[makeQuery(id+"F10.opExtrude","CAP_FACE",FACE,{"disambiguationData":[OSD([sQuery(id+"F9.wireOp",EDGE,"E4.bottom"),sQuery(id+"F9.wireOp",EDGE,"E4.top"),sQuery(id+"F9.wireOp",EDGE,"E4.left"),sQuery(id+"F9.wireOp",EDGE,"E4.right")])],"isStart":false}),makeQuery(id+"F12.opExtrude","SWEPT_FACE",FACE,{"disambiguationData":[OSD([sQuery(id+"F11.wireOp",EDGE,"E11.MirrorCS")])]})]});
            fillet(context, id + "F19", {"entities" : qUnion([Q0, Q1, Q2, Q3, Q4, Q5, Q6, Q7, Q8, Q9, Q10, Q11, Q12, Q13, Q14, Q15, Q16, Q17, Q18, Q19, Q20, Q21, Q22, Q23]), "radius" : 1 * mm, "tangentPropagation" : true, "allowEdgeOverflow" : false});
        }
        {
            var Q0;
            Q0=makeQuery(id+"F10.opExtrude","SWEPT_EDGE",EDGE,{"disambiguationData":[OSD([sQuery(id+"F9.wireOp",EDGE,"E4.top"),sQuery(id+"F9.wireOp",EDGE,"E4.right")])]});
            var Q1;
            Q1=makeQuery(id+"F10.opExtrude","SWEPT_EDGE",EDGE,{"disambiguationData":[OSD([sQuery(id+"F9.wireOp",EDGE,"E4.top"),sQuery(id+"F9.wireOp",EDGE,"E4.left")])]});
            var Q2;
            Q2=makeQuery(id+"F10.opExtrude","SWEPT_EDGE",EDGE,{"disambiguationData":[OSD([sQuery(id+"F9.wireOp",EDGE,"E4.bottom"),sQuery(id+"F9.wireOp",EDGE,"E4.left")])]});
            var Q3;
            Q3=makeQuery(id+"F10.opExtrude","SWEPT_EDGE",EDGE,{"disambiguationData":[OSD([sQuery(id+"F9.wireOp",EDGE,"E4.bottom"),sQuery(id+"F9.wireOp",EDGE,"E4.right")])]});
            var Q4;
            Q4=makeQuery(id+"F10.opExtrude","CAP_EDGE",EDGE,{"disambiguationData":[OSD([sQuery(id+"F9.wireOp",EDGE,"E4.top")])],"isStart":false});
            var Q5;
            Q5=makeQuery(id+"F10.opExtrude","CAP_EDGE",EDGE,{"disambiguationData":[OSD([sQuery(id+"F9.wireOp",EDGE,"E4.right")])],"isStart":false});
            var Q6;
            Q6=makeQuery(id+"F10.opExtrude","CAP_EDGE",EDGE,{"disambiguationData":[OSD([sQuery(id+"F9.wireOp",EDGE,"E4.bottom")])],"isStart":false});
            var Q7;
            Q7=makeQuery(id+"F10.opExtrude","CAP_EDGE",EDGE,{"disambiguationData":[OSD([sQuery(id+"F9.wireOp",EDGE,"E4.left")])],"isStart":false});
            fillet(context, id + "F20", {"entities" : qUnion([Q0, Q1, Q2, Q3, Q4, Q5, Q6, Q7]), "radius" : 5 * mm, "tangentPropagation" : true, "allowEdgeOverflow" : false});
        }
        {
            var Q0;
            Q0=makeQuery(id+"F10.opExtrude","CAP_FACE",FACE,{"disambiguationData":[OSD([sQuery(id+"F9.wireOp",EDGE,"E4.bottom"),sQuery(id+"F9.wireOp",EDGE,"E4.top"),sQuery(id+"F9.wireOp",EDGE,"E4.left"),sQuery(id+"F9.wireOp",EDGE,"E4.right")])],"isStart":true});
            var sketch = newSketch(context, id + "F21", { "sketchPlane" : qUnion([Q0])});
            skArc(sketch, "E33.0", {"start": v(-112.63, 0) * mm, "mid": v(-109.1, 1.46) * mm, "end": v(-107.63, 5) * mm});
            skLineSegment(sketch, "E33.1", {"start": v(-262.63, 0) * mm, "end": v(-112.63, 0) * mm});
            skLineSegment(sketch, "E33.2", {"start": v(-107.63, 5) * mm, "end": v(-107.63, 85) * mm});
            skArc(sketch, "E33.3", {"start": v(-267.63, 5) * mm, "mid": v(-266.17, 1.46) * mm, "end": v(-262.63, 0) * mm});
            skArc(sketch, "E33.4", {"start": v(-107.63, 85) * mm, "mid": v(-109.1, 88.54) * mm, "end": v(-112.63, 90) * mm});
            skLineSegment(sketch, "E33.5", {"start": v(-112.63, 90) * mm, "end": v(-262.63, 90) * mm});
            skArc(sketch, "E33.6", {"start": v(-262.63, 90) * mm, "mid": v(-266.17, 88.54) * mm, "end": v(-267.63, 85) * mm});
            skLineSegment(sketch, "E33.7", {"start": v(-267.63, 85) * mm, "end": v(-267.63, 5) * mm});
            skSolve(sketch);
        }
        {
            var Q0;
            Q0 = qSketchRegion(id + "F21", true);
            extrude(context, id + "F22", {"entities" : qUnion([Q0]), "operationType" : NewBodyOperationType.ADD, "depth" : 1 * mm, "offsetDistance" : 25 * mm});
        }
    });
